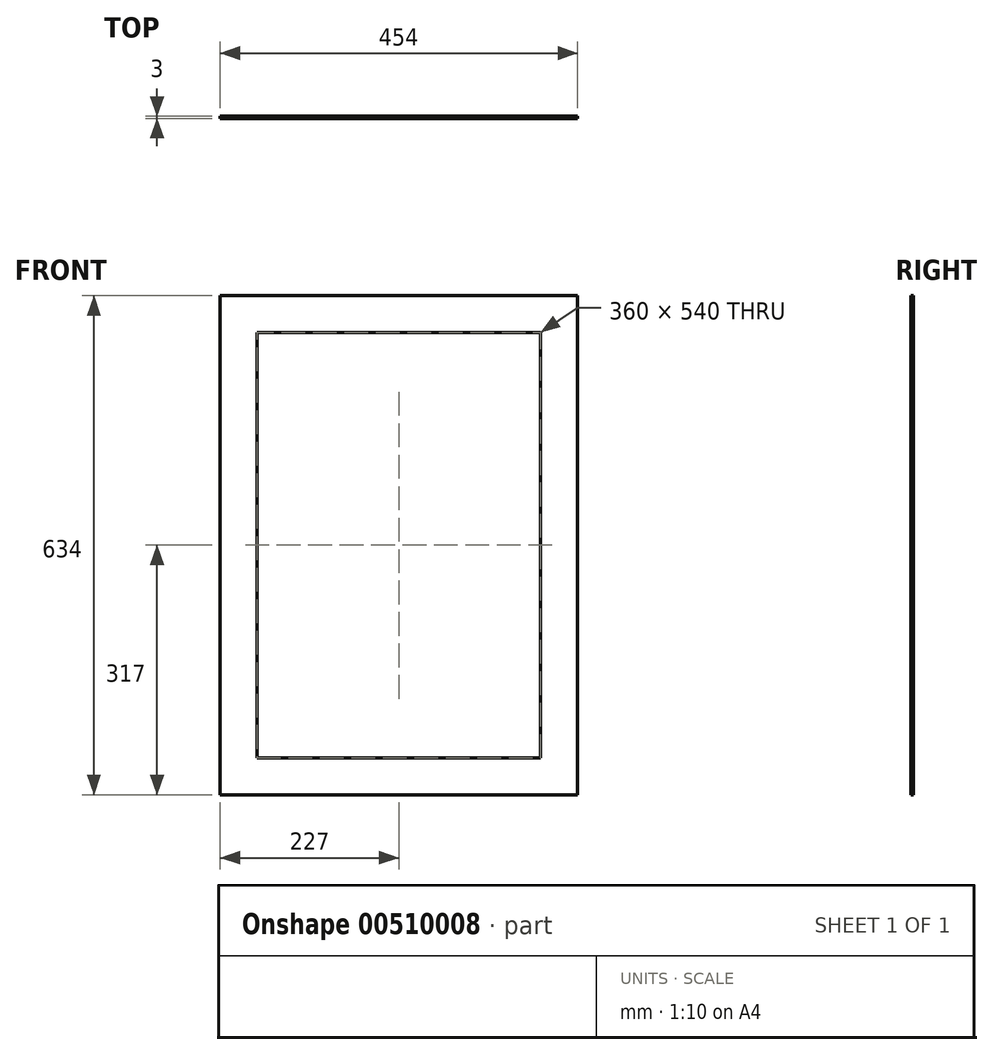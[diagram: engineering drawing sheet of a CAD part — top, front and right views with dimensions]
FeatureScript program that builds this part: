
annotation { "Feature Type Name" : "Feature", "Feature Type Description" : "" }
export const myFeature = defineFeature(function(context is Context, id is Id, definition is map)
    precondition{}
    {
        {
            var Q0;
            Q0=qCreatedBy(makeId("Front.planeOp"),FACE);
            var sketch = newSketch(context, id + "F0", { "sketchPlane" : qUnion([Q0])});
            skLineSegment(sketch, "E0.bottom", {"start": v(-180, 270) * mm, "end": v(180, 270) * mm});
            skLineSegment(sketch, "E0.top", {"start": v(-180, -270) * mm, "end": v(180, -270) * mm});
            skLineSegment(sketch, "E0.left", {"start": v(-180, 270) * mm, "end": v(-180, -270) * mm});
            skLineSegment(sketch, "E0.right", {"start": v(180, 270) * mm, "end": v(180, -270) * mm});
            skLineSegment(sketch, "E1", {"start": v(-180, 270) * mm, "end": v(180, -270) * mm, "construction": true});
            skLineSegment(sketch, "E2.0", {"start": v(-227, 317) * mm, "end": v(227, 317) * mm});
            skLineSegment(sketch, "E2.1", {"start": v(-227, 317) * mm, "end": v(-227, -317) * mm});
            skLineSegment(sketch, "E2.2", {"start": v(-227, -317) * mm, "end": v(227, -317) * mm});
            skLineSegment(sketch, "E2.3", {"start": v(227, 317) * mm, "end": v(227, -317) * mm});
            skSolve(sketch);
        }
        {
            var Q0;
            Q0 = qSketchRegion(id + "F0", true);
            extrude(context, id + "F1", {"entities" : qUnion([Q0]), "depth" : 3 * mm});
        }
    });
